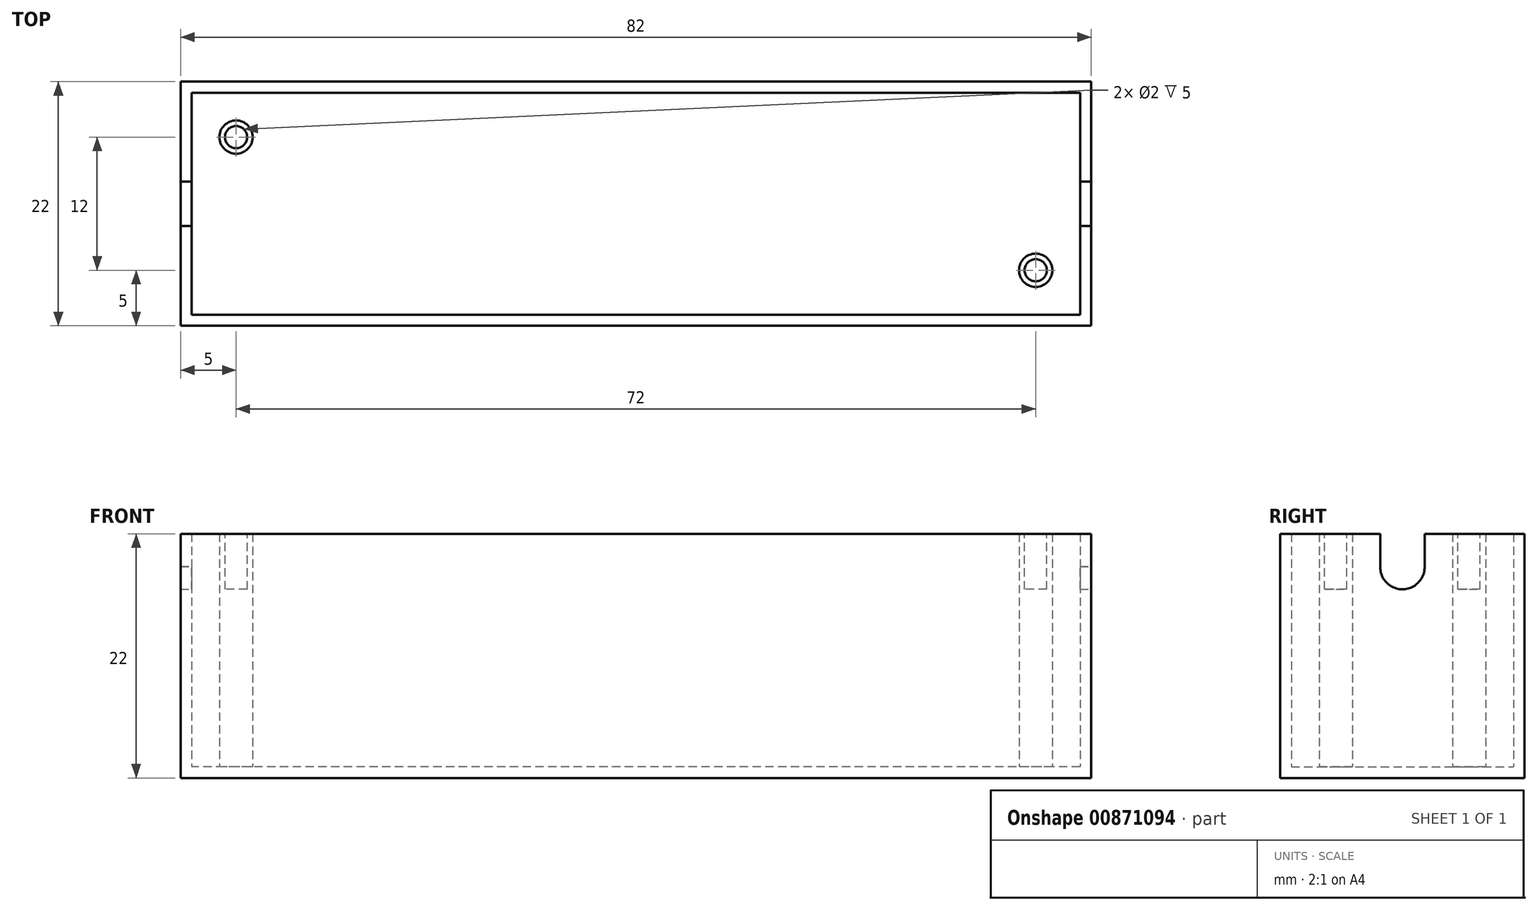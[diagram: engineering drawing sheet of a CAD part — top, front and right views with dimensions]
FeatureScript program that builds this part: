
annotation { "Feature Type Name" : "Feature", "Feature Type Description" : "" }
export const myFeature = defineFeature(function(context is Context, id is Id, definition is map)
    precondition{}
    {
        {
            var Q0;
            Q0=qCreatedBy(makeId("Top.planeOp"),FACE);
            var sketch = newSketch(context, id + "F0", { "sketchPlane" : qUnion([Q0])});
            skLineSegment(sketch, "E0.bottom", {"start": v(40, -10) * mm, "end": v(-40, -10) * mm});
            skLineSegment(sketch, "E0.top", {"start": v(40, 10) * mm, "end": v(-40, 10) * mm});
            skLineSegment(sketch, "E0.left", {"start": v(40, -10) * mm, "end": v(40, 10) * mm});
            skLineSegment(sketch, "E0.right", {"start": v(-40, -10) * mm, "end": v(-40, 10) * mm});
            skPoint(sketch, "E0.middle", {"position": v(0, 0) * mm});
            skLineSegment(sketch, "E1.0", {"start": v(41, 11) * mm, "end": v(-41, 11) * mm});
            skLineSegment(sketch, "E1.1", {"start": v(41, -11) * mm, "end": v(41, 11) * mm});
            skLineSegment(sketch, "E1.2", {"start": v(41, -11) * mm, "end": v(-41, -11) * mm});
            skLineSegment(sketch, "E1.3", {"start": v(-41, -11) * mm, "end": v(-41, 11) * mm});
            skCircle(sketch, "E2", {"center": v(-36, 6) * mm, "radius": 1.5 * mm});
            skCircle(sketch, "E3.MirrorC", {"center": v(36, -6) * mm, "radius": 1.5 * mm});
            skSolve(sketch);
        }
        {
            var Q0;
            Q0=makeQuery(id+"F0.imprint","IMPRINT",FACE,{"disambiguationData":[TD([[makeQuery(id+"F0.imprint","IMPRINT",EDGE,{"derivedFrom":sQuery(id+"F0.wireOp",EDGE,"E0.bottom")}),-1.0]])]});
            extrude(context, id + "F1", {"entities" : qUnion([Q0]), "depth" : 1 * mm, "offsetDistance" : 25 * mm});
        }
        {
            var Q0;
            Q0=makeQuery(id+"F0.imprint","IMPRINT",FACE,{"disambiguationData":[TD([[makeQuery(id+"F0.imprint","IMPRINT",EDGE,{"derivedFrom":sQuery(id+"F0.wireOp",EDGE,"E0.bottom")}),1.0]])]});
            var Q1;
            Q1=makeQuery(id+"F0.imprint","IMPRINT",FACE,{"disambiguationData":[TD([[makeQuery(id+"F0.imprint","IMPRINT",EDGE,{"derivedFrom":sQuery(id+"F0.wireOp",EDGE,"E2")}),1.0]])]});
            var Q2;
            Q2=makeQuery(id+"F0.imprint","IMPRINT",FACE,{"disambiguationData":[TD([[makeQuery(id+"F0.imprint","IMPRINT",EDGE,{"derivedFrom":sQuery(id+"F0.wireOp",EDGE,"E3.MirrorC")}),1.0]])]});
            extrude(context, id + "F2", {"entities" : qUnion([Q0, Q1, Q2]), "operationType" : NewBodyOperationType.ADD, "depth" : 22 * mm, "offsetDistance" : 25 * mm});
        }
        {
            var Q0;
            Q0=makeQuery(id+"F2.opExtrude","CAP_FACE",FACE,{"disambiguationData":[OSD([sQuery(id+"F0.wireOp",EDGE,"E2")])],"isStart":false});
            var sketch = newSketch(context, id + "F3", { "sketchPlane" : qUnion([Q0])});
            skCircle(sketch, "E4", {"center": v(-36, 6) * mm, "radius": 1 * mm});
            skCircle(sketch, "E5.MirrorC", {"center": v(36, -6) * mm, "radius": 1 * mm});
            skSolve(sketch);
        }
        {
            var Q0;
            Q0=makeQuery(id+"F3.imprint","IMPRINT",FACE,{"disambiguationData":[TD([[makeQuery(id+"F3.imprint","IMPRINT",EDGE,{"derivedFrom":sQuery(id+"F3.wireOp",EDGE,"E5.MirrorC")}),1.0]])]});
            var Q1;
            Q1=makeQuery(id+"F3.imprint","IMPRINT",FACE,{"disambiguationData":[TD([[makeQuery(id+"F3.imprint","IMPRINT",EDGE,{"derivedFrom":sQuery(id+"F3.wireOp",EDGE,"E4")}),1.0]])]});
            extrude(context, id + "F4", {"entities" : qUnion([Q0, Q1]), "operationType" : NewBodyOperationType.REMOVE, "oppositeDirection" : true, "depth" : 5 * mm, "offsetDistance" : 25 * mm});
        }
        {
            var Q0;
            Q0=makeQuery(id+"F2.opExtrude","SWEPT_FACE",FACE,{"disambiguationData":[OSD([sQuery(id+"F0.wireOp",EDGE,"E1.1")])]});
            var sketch = newSketch(context, id + "F5", { "sketchPlane" : qUnion([Q0])});
            skArc(sketch, "E6", {"start": v(-2, 19.08) * mm, "mid": v(-0.02, 17) * mm, "end": v(2, 19.03) * mm});
            skLineSegment(sketch, "E7", {"start": v(-2, 19.08) * mm, "end": v(-2, 22) * mm});
            skLineSegment(sketch, "E8", {"start": v(2, 19.03) * mm, "end": v(2, 22) * mm});
            skLineSegment(sketch, "E9", {"start": v(-2, 22) * mm, "end": v(2, 22) * mm});
            skSolve(sketch);
        }
        {
            var Q0;
            Q0=makeQuery(id+"F5.imprint","IMPRINT",FACE,{"disambiguationData":[TD([[makeQuery(id+"F5.imprint","IMPRINT",EDGE,{"derivedFrom":sQuery(id+"F5.wireOp",EDGE,"E6")}),1.0]])]});
            extrude(context, id + "F6", {"entities" : qUnion([Q0]), "operationType" : NewBodyOperationType.REMOVE, "oppositeDirection" : true, "depth" : 100 * mm, "offsetDistance" : 25 * mm});
        }
    });
